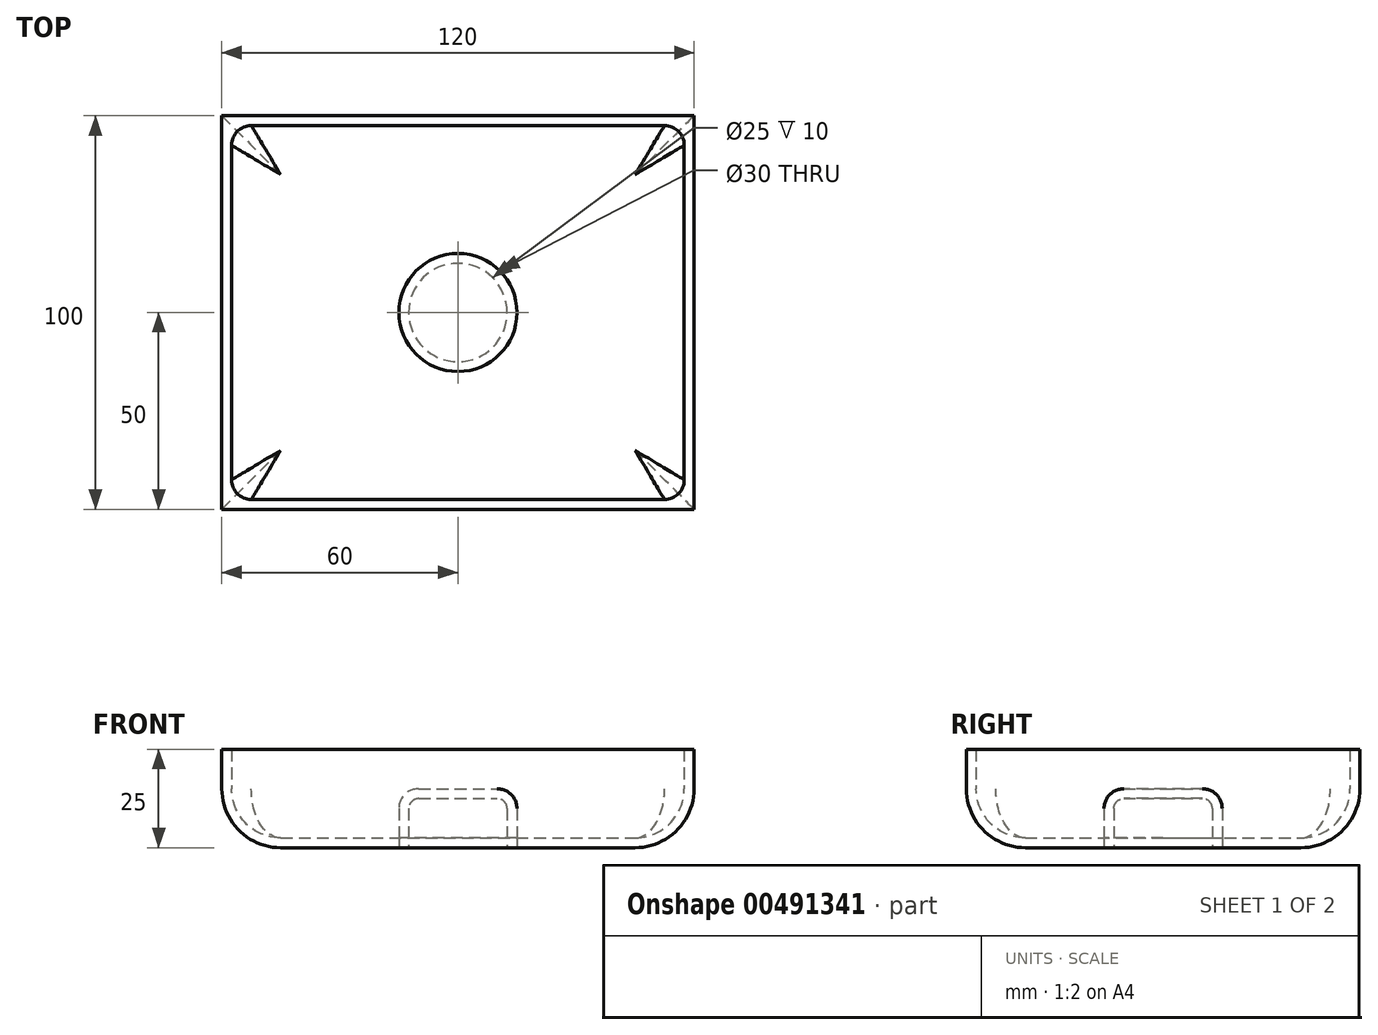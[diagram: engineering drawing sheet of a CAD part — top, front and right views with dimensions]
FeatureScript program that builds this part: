
annotation { "Feature Type Name" : "Feature", "Feature Type Description" : "" }
export const myFeature = defineFeature(function(context is Context, id is Id, definition is map)
    precondition{}
    {
        {
            var Q0;
            Q0=qCreatedBy(makeId("Top.planeOp"),FACE);
            var sketch = newSketch(context, id + "F0", { "sketchPlane" : qUnion([Q0])});
            skLineSegment(sketch, "E0.bottom", {"start": v(60, 50) * mm, "end": v(-60, 50) * mm});
            skLineSegment(sketch, "E0.top", {"start": v(60, -50) * mm, "end": v(-60, -50) * mm});
            skLineSegment(sketch, "E0.left", {"start": v(60, 50) * mm, "end": v(60, -50) * mm});
            skLineSegment(sketch, "E0.right", {"start": v(-60, 50) * mm, "end": v(-60, -50) * mm});
            skPoint(sketch, "E0.middle", {"position": v(0, 0) * mm});
            skSolve(sketch);
        }
        {
            var Q0;
            Q0 = qSketchRegion(id + "F0", true);
            extrude(context, id + "F1", {"entities" : qUnion([Q0]), "depth" : 25 * mm});
        }
        {
            var Q0;
            Q0=makeQuery(id+"F1.opExtrude","CAP_EDGE",EDGE,{"disambiguationData":[OSD([sQuery(id+"F0.wireOp",EDGE,"E0.right")])],"isStart":true});
            var Q1;
            Q1=makeQuery(id+"F1.opExtrude","CAP_EDGE",EDGE,{"disambiguationData":[OSD([sQuery(id+"F0.wireOp",EDGE,"E0.top")])],"isStart":true});
            var Q2;
            Q2=makeQuery(id+"F1.opExtrude","CAP_EDGE",EDGE,{"disambiguationData":[OSD([sQuery(id+"F0.wireOp",EDGE,"E0.left")])],"isStart":true});
            var Q3;
            Q3=makeQuery(id+"F1.opExtrude","CAP_EDGE",EDGE,{"disambiguationData":[OSD([sQuery(id+"F0.wireOp",EDGE,"E0.bottom")])],"isStart":true});
            fillet(context, id + "F2", {"entities" : qUnion([Q0, Q1, Q2, Q3]), "radius" : 15 * mm, "tangentPropagation" : true, "allowEdgeOverflow" : false});
        }
        {
            var Q0;
            Q0=makeQuery(id+"F1.opExtrude","CAP_FACE",FACE,{"disambiguationData":[OSD([sQuery(id+"F0.wireOp",EDGE,"E0.bottom"),sQuery(id+"F0.wireOp",EDGE,"E0.top"),sQuery(id+"F0.wireOp",EDGE,"E0.left"),sQuery(id+"F0.wireOp",EDGE,"E0.right")])],"isStart":true});
            var sketch = newSketch(context, id + "F3", { "sketchPlane" : qUnion([Q0])});
            skCircle(sketch, "E1", {"center": v(0, 0) * mm, "radius": 15 * mm});
            skSolve(sketch);
        }
        {
            var Q0;
            Q0=makeQuery(id+"F3.imprint","IMPRINT",FACE,{"disambiguationData":[TD([[makeQuery(id+"F3.imprint","IMPRINT",EDGE,{"derivedFrom":sQuery(id+"F3.wireOp",EDGE,"E1")}),1.0]])]});
            extrude(context, id + "F4", {"entities" : qUnion([Q0]), "depth" : 0 * mm, "hasSecondDirection" : true, "secondDirectionOppositeDirection" : true, "secondDirectionDepth" : 15 * mm});
        }
        {
            var Q0;
            Q0=makeQuery(id+"F4.opExtrude","CAP_EDGE",EDGE,{"disambiguationData":[OSD([sQuery(id+"F3.wireOp",EDGE,"E1")])],"isStart":true});
            fillet(context, id + "F5", {"entities" : qUnion([Q0]), "radius" : 5 * mm, "tangentPropagation" : true, "allowEdgeOverflow" : false});
        }
        {
            var Q0;
            Q0=makeQuery(id+"F1.opExtrude","CAP_FACE",FACE,{"disambiguationData":[OSD([sQuery(id+"F0.wireOp",EDGE,"E0.bottom"),sQuery(id+"F0.wireOp",EDGE,"E0.top"),sQuery(id+"F0.wireOp",EDGE,"E0.left"),sQuery(id+"F0.wireOp",EDGE,"E0.right")])],"isStart":false});
            shell(context, id + "F6", {"entities" : qUnion([Q0]), "thickness" : 2.5 * mm});
        }
        {
            var Q0;
            Q0=makeQuery(id+"F4.opExtrude","SWEPT_BODY",BODY,{"disambiguationData":[OSD([sQuery(id+"F3.wireOp",EDGE,"E1")])]});
            var Q1;
            Q1=makeQuery(id+"F1.opExtrude","SWEPT_BODY",BODY,{"disambiguationData":[OSD([sQuery(id+"F0.wireOp",EDGE,"E0.bottom"),sQuery(id+"F0.wireOp",EDGE,"E0.top"),sQuery(id+"F0.wireOp",EDGE,"E0.left"),sQuery(id+"F0.wireOp",EDGE,"E0.right")])]});
            booleanBodies(context, id + "F7", {"operationType" : BooleanOperationType.SUBTRACTION, "tools" : qUnion([Q0]), "targets" : qUnion([Q1]), "keepTools" : true});
        }
        {
            var Q0;
            Q0=makeQuery(id+"F4.opExtrude","CAP_FACE",FACE,{"disambiguationData":[OSD([sQuery(id+"F3.wireOp",EDGE,"E1")])],"isStart":false});
            shell(context, id + "F8", {"entities" : qUnion([Q0]), "thickness" : 2.5 * mm});
        }
        {
            var Q0;
            {var subQ0=sQuery(id+"F0.wireOp",EDGE,"E0.right");var subQ1=sQuery(id+"F0.wireOp",EDGE,"E0.bottom");Q0=makeQuery(id+"F6.opShell","OFFSET_EDGE",EDGE,{"disambiguationData":[OSD([subQ1,subQ0]),TDD([makeQuery(id+"F1.opExtrude","SWEPT_EDGE",EDGE,{"disambiguationData":[OSD([subQ1,subQ0])]})])]});}
            var Q1;
            {var subQ0=sQuery(id+"F0.wireOp",EDGE,"E0.left");var subQ1=sQuery(id+"F0.wireOp",EDGE,"E0.bottom");Q1=makeQuery(id+"F6.opShell","OFFSET_EDGE",EDGE,{"disambiguationData":[OSD([subQ1,subQ0]),TDD([makeQuery(id+"F1.opExtrude","SWEPT_EDGE",EDGE,{"disambiguationData":[OSD([subQ1,subQ0])]})])]});}
            var Q2;
            {var subQ0=sQuery(id+"F0.wireOp",EDGE,"E0.left");var subQ1=sQuery(id+"F0.wireOp",EDGE,"E0.top");Q2=makeQuery(id+"F6.opShell","OFFSET_EDGE",EDGE,{"disambiguationData":[OSD([subQ1,subQ0]),TDD([makeQuery(id+"F1.opExtrude","SWEPT_EDGE",EDGE,{"disambiguationData":[OSD([subQ1,subQ0])]})])]});}
            var Q3;
            {var subQ0=sQuery(id+"F0.wireOp",EDGE,"E0.right");var subQ1=sQuery(id+"F0.wireOp",EDGE,"E0.top");Q3=makeQuery(id+"F6.opShell","OFFSET_EDGE",EDGE,{"disambiguationData":[OSD([subQ1,subQ0]),TDD([makeQuery(id+"F1.opExtrude","SWEPT_EDGE",EDGE,{"disambiguationData":[OSD([subQ1,subQ0])]})])]});}
            fillet(context, id + "F9", {"entities" : qUnion([Q0, Q1, Q2, Q3]), "radius" : 5 * mm, "tangentPropagation" : true, "allowEdgeOverflow" : false});
        }
        {
            var Q0;
            Q0=sQuery(id+"F0.wireOp",VERTEX,"E0.middle");
            var Q1;
            Q1=makeQuery(id+"F1.opExtrude","SWEPT_BODY",BODY,{"disambiguationData":[OSD([sQuery(id+"F0.wireOp",EDGE,"E0.bottom"),sQuery(id+"F0.wireOp",EDGE,"E0.top"),sQuery(id+"F0.wireOp",EDGE,"E0.left"),sQuery(id+"F0.wireOp",EDGE,"E0.right")])]});
            hole(context, id + "F10", {"style" : HoleStyle.SIMPLE, "endStyle" : HoleEndStyle.THROUGH, "oppositeDirection" : true, "holeDiameter" : 8 * mm, "isTappedThrough" : true, "tappedDepth" : 12 * mm, "tapClearance" : 3, "locations" : qUnion([Q0]), "scope" : qUnion([Q1])});
        }
    });
